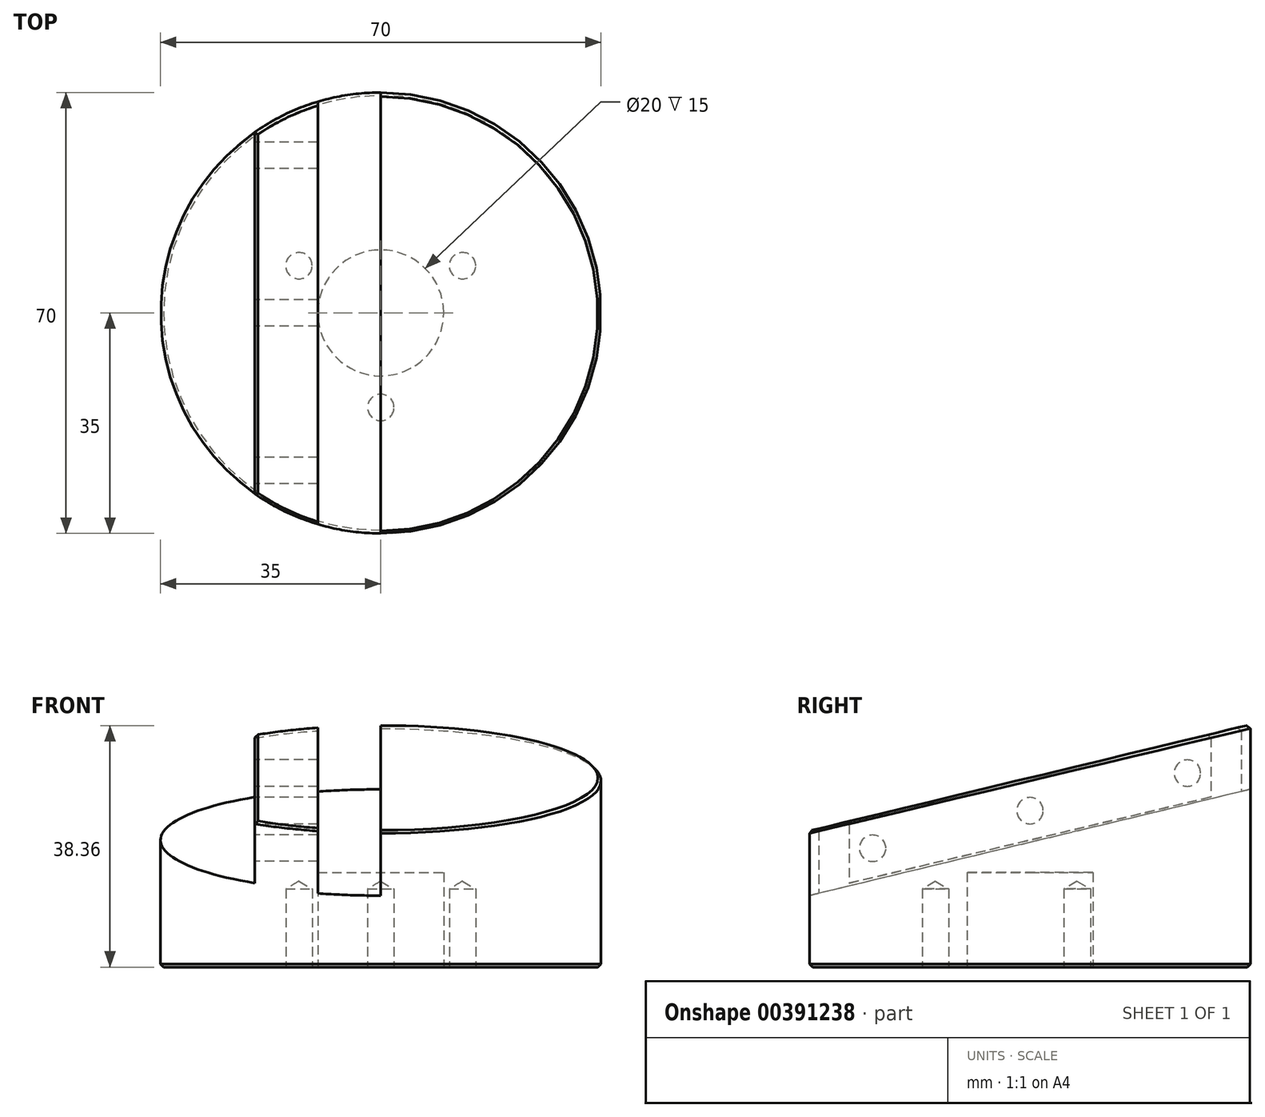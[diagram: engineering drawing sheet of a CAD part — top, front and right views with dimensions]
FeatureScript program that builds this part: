
annotation { "Feature Type Name" : "Feature", "Feature Type Description" : "" }
export const myFeature = defineFeature(function(context is Context, id is Id, definition is map)
    precondition{}
    {
        {
            var Q0;
            Q0=qCreatedBy(makeId("Right.planeOp"),FACE);
            var sketch = newSketch(context, id + "F0", { "sketchPlane" : qUnion([Q0])});
            skLineSegment(sketch, "E0", {"start": v(35, 0) * mm, "end": v(35, 31.44) * mm});
            skLineSegment(sketch, "E1", {"start": v(35, 31.44) * mm, "end": v(0, 31.44) * mm});
            skLineSegment(sketch, "E2", {"start": v(0, 31.44) * mm, "end": v(0, 0) * mm});
            skLineSegment(sketch, "E3", {"start": v(0, -5.74) * mm, "end": v(0, 39.91) * mm, "construction": true});
            skPoint(sketch, "E3.endSnap0", {"position": v(0, 15.72) * mm});
            skLineSegment(sketch, "E4", {"start": v(35, 0) * mm, "end": v(35, -8.56) * mm});
            skLineSegment(sketch, "E5", {"start": v(35, -8.56) * mm, "end": v(0, -8.56) * mm});
            skLineSegment(sketch, "E6", {"start": v(0, -8.56) * mm, "end": v(0, 0) * mm});
            skSolve(sketch);
        }
        {
            var Q0;
            Q0 = qSketchRegion(id + "F0", true);
            var Q1;
            Q1=sQuery(id+"F0.wireOp",EDGE,"E3");
            revolve(context, id + "F1", {"entities" : qUnion([Q0]), "axis" : qUnion([Q1]), "revolveType" : RevolveType.FULL});
        }
        {
            var Q0;
            Q0=qCreatedBy(makeId("Right.planeOp"),FACE);
            cPlane(context, id + "F2", {"entities" : qUnion([Q0]), "cplaneType" : CPlaneType.OFFSET, "offset" : 25 * mm, "width" : 150 * mm, "height" : 150 * mm});
        }
        {
            var Q0;
            Q0=qCreatedBy(id+"F2.planeOp",FACE);
            cPlane(context, id + "F3", {"entities" : qUnion([Q0]), "cplaneType" : CPlaneType.OFFSET, "offset" : 25 * mm, "width" : 150 * mm, "height" : 150 * mm});
        }
        {
            var Q0;
            Q0=qCreatedBy(id+"F3.planeOp",FACE);
            var sketch = newSketch(context, id + "F4", { "sketchPlane" : qUnion([Q0])});
            skLineSegment(sketch, "E7", {"start": v(-41.03, 11.63) * mm, "end": v(44.21, 32.17) * mm});
            skLineSegment(sketch, "E8", {"start": v(44.21, 32.17) * mm, "end": v(-40.78, 32.17) * mm});
            skLineSegment(sketch, "E9", {"start": v(-40.78, 32.17) * mm, "end": v(-41.03, 11.63) * mm});
            skSolve(sketch);
        }
        {
            var Q0;
            Q0 = qSketchRegion(id + "F4", true);
            extrude(context, id + "F5", {"entities" : qUnion([Q0]), "operationType" : NewBodyOperationType.REMOVE, "endBound" : BoundingType.THROUGH_ALL, "oppositeDirection" : true, "depth" : 25 * mm});
        }
        {
            var Q0;
            Q0=makeQuery(id+"F5.boolean.opBoolean","COPY",FACE,{"derivedFrom":makeQuery(id+"F5.opExtrude","SWEPT_FACE",FACE,{"disambiguationData":[OSD([sQuery(id+"F4.wireOp",EDGE,"E7")])]})});
            var sketch = newSketch(context, id + "F6", { "sketchPlane" : qUnion([Q0])});
            skLineSegment(sketch, "E10", {"start": v(0, 43.1) * mm, "end": v(0, -47.54) * mm, "construction": true});
            skLineSegment(sketch, "E11", {"start": v(-36.67, 0) * mm, "end": v(36.67, 0) * mm, "construction": true});
            skLineSegment(sketch, "E12.bottom", {"start": v(0, 43.1) * mm, "end": v(-10, 43.1) * mm});
            skLineSegment(sketch, "E12.top", {"start": v(0, -41.95) * mm, "end": v(-10, -41.95) * mm});
            skLineSegment(sketch, "E12.left", {"start": v(0, 43.1) * mm, "end": v(0, -41.95) * mm});
            skLineSegment(sketch, "E12.right", {"start": v(-10, 43.1) * mm, "end": v(-10, -41.95) * mm});
            skSolve(sketch);
        }
        {
            var Q0;
            Q0 = qSketchRegion(id + "F6", true);
            extrude(context, id + "F7", {"entities" : qUnion([Q0]), "operationType" : NewBodyOperationType.REMOVE, "oppositeDirection" : true, "depth" : 10 * mm});
        }
        {
            var Q0;
            Q0=makeQuery(id+"F1.opRevolve","SWEPT_FACE",FACE,{"disambiguationData":[OSD([sQuery(id+"F0.wireOp",EDGE,"E5")])]});
            var sketch = newSketch(context, id + "F8", { "sketchPlane" : qUnion([Q0])});
            skCircle(sketch, "E13", {"center": v(0, 0) * mm, "radius": 10 * mm});
            skSolve(sketch);
        }
        {
            var Q0;
            Q0 = qSketchRegion(id + "F8", true);
            extrude(context, id + "F9", {"entities" : qUnion([Q0]), "operationType" : NewBodyOperationType.REMOVE, "oppositeDirection" : true, "depth" : 15 * mm});
        }
        {
            var Q0;
            Q0=makeQuery(id+"F1.opRevolve","SWEPT_FACE",FACE,{"disambiguationData":[OSD([sQuery(id+"F0.wireOp",EDGE,"E5")])]});
            var sketch = newSketch(context, id + "F10", { "sketchPlane" : qUnion([Q0])});
            skCircle(sketch, "E14", {"center": v(0, 0) * mm, "radius": 15 * mm, "construction": true});
            skPoint(sketch, "E15", {"position": v(0, 15) * mm});
            skPoint(sketch, "E16.1.0", {"position": v(-13, -7.5) * mm});
            skPoint(sketch, "E16.2.0", {"position": v(13, -7.5) * mm});
            skSolve(sketch);
        }
        {
            var Q0;
            Q0=sQuery(id+"F10.wireOp",VERTEX,"E15");
            var Q1;
            Q1=sQuery(id+"F10.wireOp",VERTEX,"E16.2.0");
            var Q2;
            Q2=sQuery(id+"F10.wireOp",VERTEX,"E16.1.0");
            var Q3;
            Q3=makeQuery(id+"F1.opRevolve","SWEPT_BODY",BODY,{"disambiguationData":[OSD([sQuery(id+"F0.wireOp",EDGE,"E0"),sQuery(id+"F0.wireOp",EDGE,"E1"),sQuery(id+"F0.wireOp",EDGE,"E2"),sQuery(id+"F0.wireOp",EDGE,"E4"),sQuery(id+"F0.wireOp",EDGE,"E5"),sQuery(id+"F0.wireOp",EDGE,"E6")])]});
            hole(context, id + "F11", {"style" : HoleStyle.SIMPLE, "endStyle" : HoleEndStyle.BLIND, "standardTappedOrClearance" : lookupTablePath({ "standard" : "ISO", "engagement" : "75%", "pitch" : "0.8 mm", "size" : "M5", "type" : "Tapped" }), "standardBlindInLast" : lookupTablePath({ "standard" : "ISO", "engagement" : "75%", "pitch" : "0.8 mm", "size" : "M5", "type" : "Tapped" }), "holeDiameter" : 4.2 * mm, "showTappedDepth" : true, "holeDepth" : 12.4 * mm, "isTappedThrough" : true, "tappedDepth" : 10 * mm, "tapClearance" : 3, "startFromSketch" : true, "locations" : qUnion([Q0, Q1, Q2]), "scope" : qUnion([Q3]), "majorDiameter" : 5 * mm});
        }
        {
            var Q0;
            Q0=makeQuery(id+"F1.opRevolve","SWEPT_EDGE",EDGE,{"disambiguationData":[OSD([sQuery(id+"F0.wireOp",EDGE,"E4"),sQuery(id+"F0.wireOp",EDGE,"E5")])]});
            var Q1;
            {var subQ0=makeQuery(id+"F1.opRevolve","SWEPT_FACE",FACE,{"disambiguationData":[OSD([sQuery(id+"F0.wireOp",EDGE,"E0"),sQuery(id+"F0.wireOp",EDGE,"E4")])]});var subQ1=makeQuery(id+"F5.opExtrude","SWEPT_FACE",FACE,{"disambiguationData":[OSD([sQuery(id+"F4.wireOp",EDGE,"E7")])]});Q1=makeQuery(id+"F7.boolean.opBoolean","SPLIT",EDGE,{"disambiguationData":[TD([makeQuery(id+"F7.opExtrude","SWEPT_FACE",FACE,{"disambiguationData":[OSD([sQuery(id+"F6.wireOp",EDGE,"E12.left")])]})])],"derivedFrom":makeQuery(id+"F5.boolean.opBoolean","INTERSECT",EDGE,{"derivedFrom":[subQ0,subQ1]})});}
            var Q2;
            {var subQ0=makeQuery(id+"F1.opRevolve","SWEPT_FACE",FACE,{"disambiguationData":[OSD([sQuery(id+"F0.wireOp",EDGE,"E0"),sQuery(id+"F0.wireOp",EDGE,"E4")])]});var subQ1=makeQuery(id+"F5.opExtrude","SWEPT_FACE",FACE,{"disambiguationData":[OSD([sQuery(id+"F4.wireOp",EDGE,"E7")])]});Q2=makeQuery(id+"F7.boolean.opBoolean","SPLIT",EDGE,{"disambiguationData":[TD([makeQuery(id+"F7.opExtrude","SWEPT_FACE",FACE,{"disambiguationData":[OSD([sQuery(id+"F6.wireOp",EDGE,"E12.right")])]})])],"derivedFrom":makeQuery(id+"F5.boolean.opBoolean","INTERSECT",EDGE,{"derivedFrom":[subQ0,subQ1]})});}
            chamfer(context, id + "F12", {"entities" : qUnion([Q0, Q1, Q2]), "width" : 0.5 * mm, "tangentPropagation" : true});
        }
        {
            var Q0;
            Q0=qCreatedBy(id+"F3.planeOp",FACE);
            cPlane(context, id + "F13", {"entities" : qUnion([Q0]), "cplaneType" : CPlaneType.OFFSET, "offset" : 80 * mm, "oppositeDirection" : true, "width" : 150 * mm, "height" : 150 * mm});
        }
        {
            var Q0;
            Q0=qCreatedBy(id+"F13.planeOp",FACE);
            cPlane(context, id + "F14", {"entities" : qUnion([Q0]), "cplaneType" : CPlaneType.OFFSET, "offset" : 10 * mm, "oppositeDirection" : true, "width" : 150 * mm, "height" : 150 * mm});
        }
        {
            var Q0;
            Q0=qCreatedBy(id+"F14.planeOp",FACE);
            var sketch = newSketch(context, id + "F15", { "sketchPlane" : qUnion([Q0])});
            skLineSegment(sketch, "E17", {"start": v(33.53, 19.6) * mm, "end": v(-33.49, 3.63) * mm});
            skLineSegment(sketch, "E18", {"start": v(-33.49, 3.63) * mm, "end": v(-33.49, 18.85) * mm});
            skLineSegment(sketch, "E19", {"start": v(-33.49, 18.85) * mm, "end": v(33.53, 32.6) * mm});
            skLineSegment(sketch, "E20", {"start": v(33.53, 32.6) * mm, "end": v(33.53, 19.6) * mm});
            skSolve(sketch);
        }
        {
            var Q0;
            Q0 = qSketchRegion(id + "F15", true);
            extrude(context, id + "F16", {"entities" : qUnion([Q0]), "operationType" : NewBodyOperationType.REMOVE, "depth" : 20 * mm});
        }
        {
            var Q0;
            Q0=makeQuery(id+"F16.boolean.opBoolean","INTERSECT",EDGE,{"derivedFrom":[makeQuery(id+"F7.boolean.opBoolean","SPLIT",FACE,{"disambiguationData":[TD([makeQuery(id+"F7.opExtrude","SWEPT_FACE",FACE,{"disambiguationData":[OSD([sQuery(id+"F6.wireOp",EDGE,"E12.right")])]})])],"derivedFrom":makeQuery(id+"F5.boolean.opBoolean","COPY",FACE,{"derivedFrom":makeQuery(id+"F5.opExtrude","SWEPT_FACE",FACE,{"disambiguationData":[OSD([sQuery(id+"F4.wireOp",EDGE,"E7")])]})})}),makeQuery(id+"F16.opExtrude","CAP_FACE",FACE,{"disambiguationData":[OSD([sQuery(id+"F15.wireOp",EDGE,"E17"),sQuery(id+"F15.wireOp",EDGE,"E18"),sQuery(id+"F15.wireOp",EDGE,"E19"),sQuery(id+"F15.wireOp",EDGE,"E20")])],"isStart":false})]});
            chamfer(context, id + "F17", {"entities" : qUnion([Q0]), "width" : 0.5 * mm, "tangentPropagation" : true});
        }
        {
            var Q0;
            Q0=makeQuery(id+"F16.boolean.opBoolean","COPY",FACE,{"derivedFrom":makeQuery(id+"F16.opExtrude","CAP_FACE",FACE,{"disambiguationData":[OSD([sQuery(id+"F15.wireOp",EDGE,"E17"),sQuery(id+"F15.wireOp",EDGE,"E18"),sQuery(id+"F15.wireOp",EDGE,"E19"),sQuery(id+"F15.wireOp",EDGE,"E20")])],"isStart":false})});
            var sketch = newSketch(context, id + "F18", { "sketchPlane" : qUnion([Q0])});
            skLineSegment(sketch, "E21", {"start": v(-28.72, 23.13) * mm, "end": v(28.72, 9.42) * mm, "construction": true});
            skLineSegment(sketch, "E22", {"start": v(0, -11.53) * mm, "end": v(0, 24.73) * mm, "construction": true});
            skPoint(sketch, "E22.endSnap0", {"position": v(0, 16.28) * mm});
            skPoint(sketch, "E23", {"position": v(-25, 22.24) * mm});
            skPoint(sketch, "E24", {"position": v(25, 10.31) * mm});
            skSolve(sketch);
        }
        {
            var Q0;
            Q0=sQuery(id+"F18.wireOp",VERTEX,"E22.endSnap0");
            var Q1;
            Q1=sQuery(id+"F18.wireOp",VERTEX,"E23");
            var Q2;
            Q2=sQuery(id+"F18.wireOp",VERTEX,"E24");
            var Q3;
            Q3=makeQuery(id+"F1.opRevolve","SWEPT_BODY",BODY,{"disambiguationData":[OSD([sQuery(id+"F0.wireOp",EDGE,"E0"),sQuery(id+"F0.wireOp",EDGE,"E1"),sQuery(id+"F0.wireOp",EDGE,"E2"),sQuery(id+"F0.wireOp",EDGE,"E4"),sQuery(id+"F0.wireOp",EDGE,"E5"),sQuery(id+"F0.wireOp",EDGE,"E6")])]});
            hole(context, id + "F19", {"style" : HoleStyle.SIMPLE, "endStyle" : HoleEndStyle.BLIND, "standardTappedOrClearance" : lookupTablePath({ "standard" : "ISO", "engagement" : "75%", "pitch" : "0.8 mm", "size" : "M5", "type" : "Tapped" }), "standardBlindInLast" : lookupTablePath({ "standard" : "ISO", "engagement" : "75%", "pitch" : "0.8 mm", "size" : "M5", "type" : "Tapped" }), "holeDiameter" : 4.2 * mm, "showTappedDepth" : true, "holeDepth" : 12.4 * mm, "isTappedThrough" : true, "tappedDepth" : 10 * mm, "tapClearance" : 3, "startFromSketch" : true, "locations" : qUnion([Q0, Q1, Q2]), "scope" : qUnion([Q3]), "majorDiameter" : 5 * mm});
        }
    });
